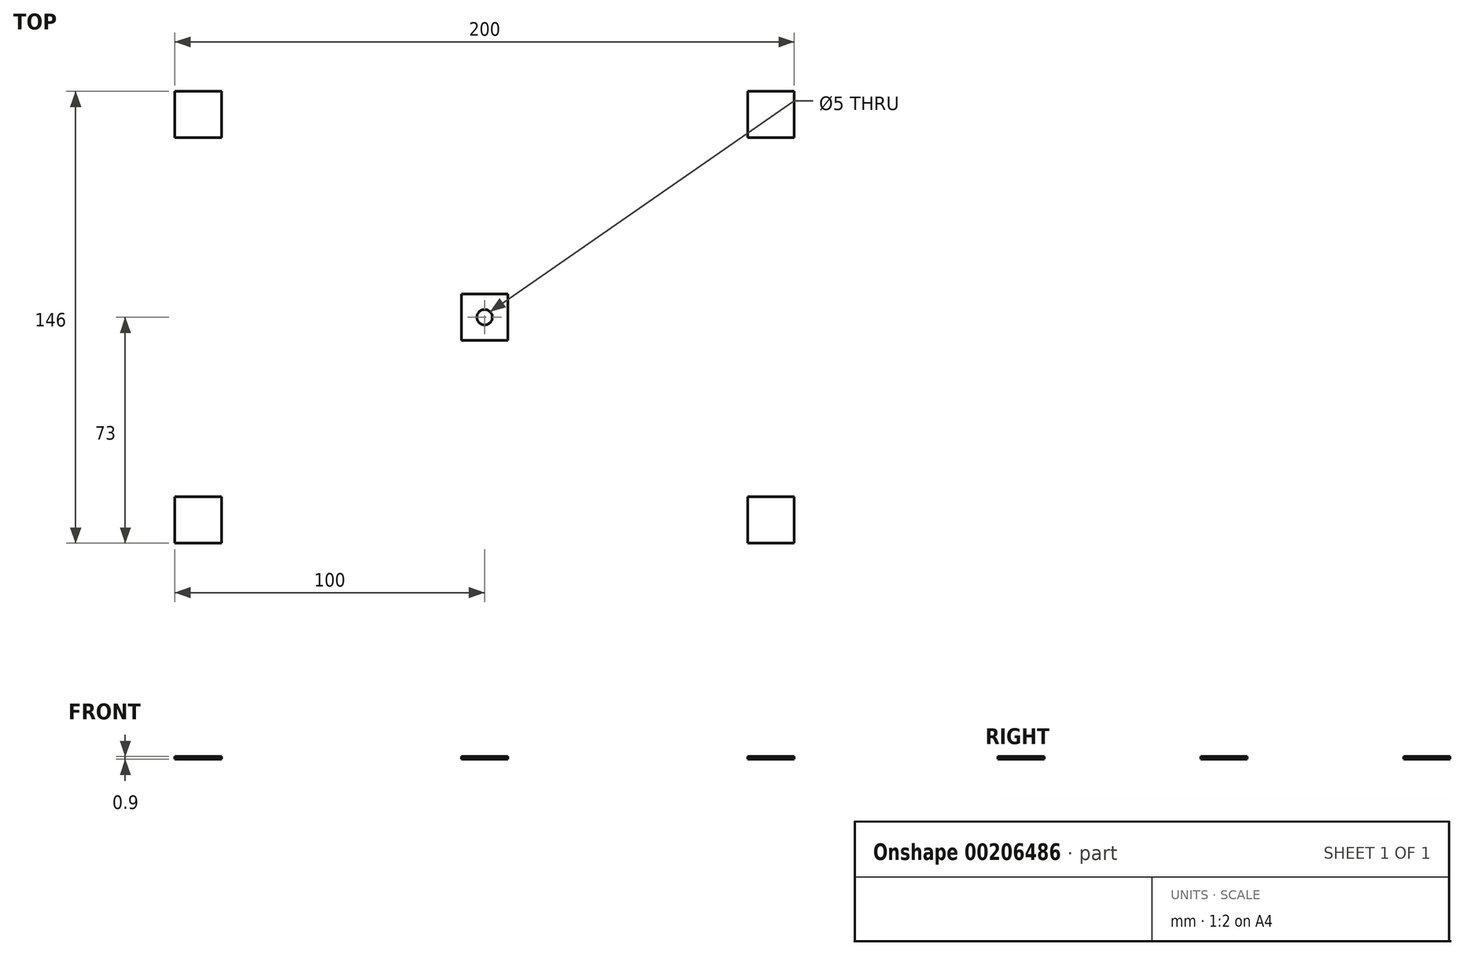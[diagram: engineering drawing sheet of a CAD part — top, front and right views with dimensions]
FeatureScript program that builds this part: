
annotation { "Feature Type Name" : "Feature", "Feature Type Description" : "" }
export const myFeature = defineFeature(function(context is Context, id is Id, definition is map)
    precondition{}
    {
        {
            var Q0;
            Q0=qCreatedBy(makeId("Top.planeOp"),FACE);
            var sketch = newSketch(context, id + "F0", { "sketchPlane" : qUnion([Q0])});
            skLineSegment(sketch, "E0.bottom", {"start": v(0, 0) * mm, "end": v(15, 0) * mm});
            skLineSegment(sketch, "E0.top", {"start": v(0, 15) * mm, "end": v(15, 15) * mm});
            skLineSegment(sketch, "E0.left", {"start": v(0, 0) * mm, "end": v(0, 15) * mm});
            skLineSegment(sketch, "E0.right", {"start": v(15, 0) * mm, "end": v(15, 15) * mm});
            skLineSegment(sketch, "E1", {"start": v(100, 0) * mm, "end": v(100, 102.54) * mm, "construction": true});
            skLineSegment(sketch, "E2", {"start": v(0, 73) * mm, "end": v(234.32, 73) * mm, "construction": true});
            skLineSegment(sketch, "E3.MirrorCS", {"start": v(185, 0) * mm, "end": v(185, 15) * mm});
            skLineSegment(sketch, "E4.MirrorCS", {"start": v(200, 15) * mm, "end": v(185, 15) * mm});
            skLineSegment(sketch, "E5.MirrorCS", {"start": v(200, 0) * mm, "end": v(185, 0) * mm});
            skLineSegment(sketch, "E6.MirrorCS", {"start": v(200, 0) * mm, "end": v(200, 15) * mm});
            skLineSegment(sketch, "E7.MirrorCS", {"start": v(200, 146) * mm, "end": v(185, 146) * mm});
            skLineSegment(sketch, "E8.MirrorCS", {"start": v(0, 131) * mm, "end": v(15, 131) * mm});
            skLineSegment(sketch, "E9.MirrorCS", {"start": v(200, 131) * mm, "end": v(185, 131) * mm});
            skLineSegment(sketch, "E10.MirrorCS", {"start": v(0, 146) * mm, "end": v(0, 131) * mm});
            skLineSegment(sketch, "E11.MirrorCS", {"start": v(15, 146) * mm, "end": v(15, 131) * mm});
            skLineSegment(sketch, "E12.MirrorCS", {"start": v(0, 146) * mm, "end": v(15, 146) * mm});
            skLineSegment(sketch, "E13.MirrorCS", {"start": v(200, 146) * mm, "end": v(200, 131) * mm});
            skLineSegment(sketch, "E14.MirrorCS", {"start": v(185, 146) * mm, "end": v(185, 131) * mm});
            skLineSegment(sketch, "E15.bottom", {"start": v(92.5, 80.5) * mm, "end": v(107.5, 80.5) * mm});
            skLineSegment(sketch, "E15.top", {"start": v(92.5, 65.5) * mm, "end": v(107.5, 65.5) * mm});
            skLineSegment(sketch, "E15.left", {"start": v(92.5, 80.5) * mm, "end": v(92.5, 65.5) * mm});
            skLineSegment(sketch, "E15.right", {"start": v(107.5, 80.5) * mm, "end": v(107.5, 65.5) * mm});
            skCircle(sketch, "E16", {"center": v(100, 73) * mm, "radius": 2.5 * mm});
            skSolve(sketch);
        }
        {
            var Q0;
            Q0 = qSketchRegion(id + "F0", true);
            extrude(context, id + "F1", {"entities" : qUnion([Q0]), "depth" : 0.9 * mm, "offsetDistance" : 25 * mm});
        }
    });
